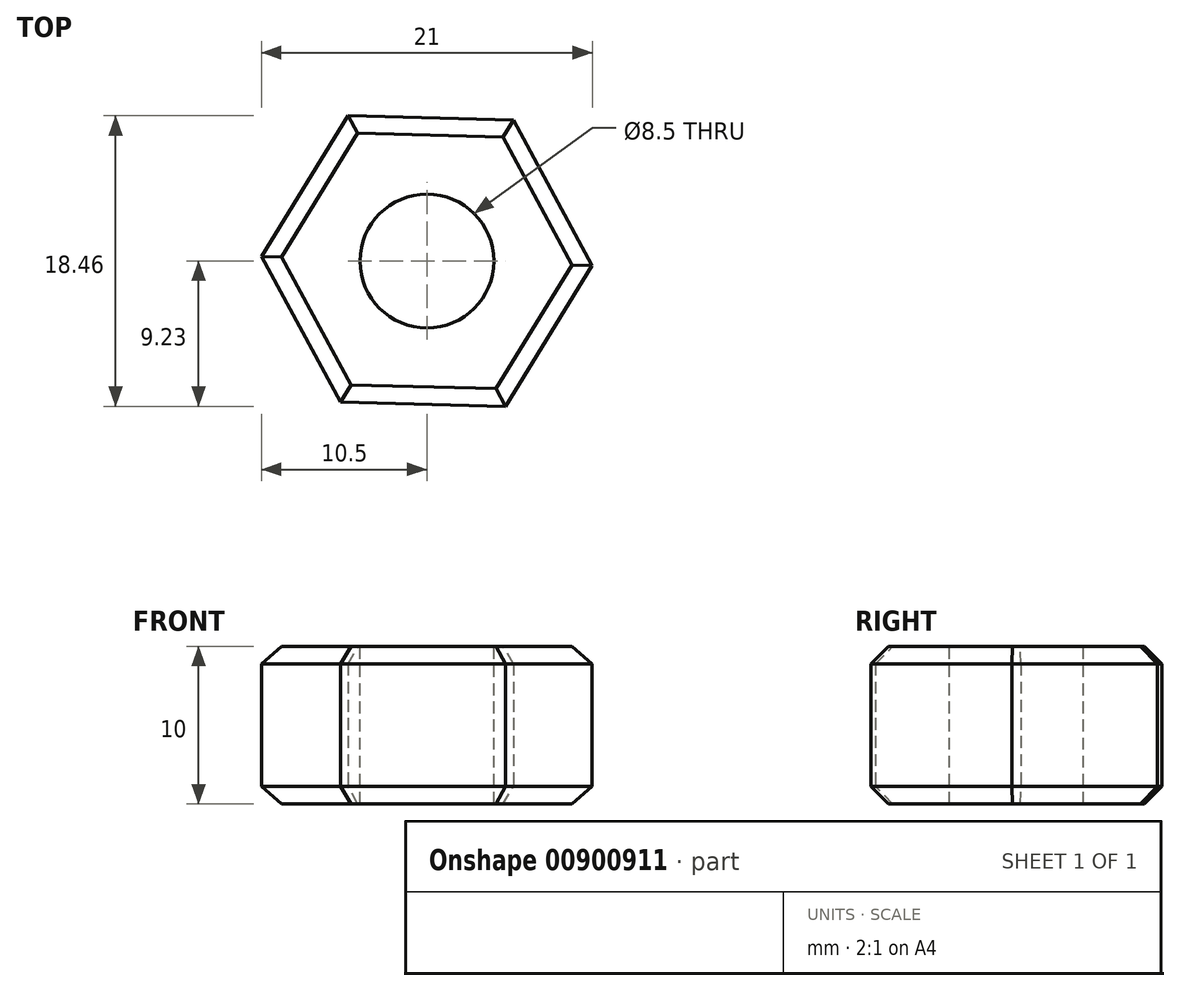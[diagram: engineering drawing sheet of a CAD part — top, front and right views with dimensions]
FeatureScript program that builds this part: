
annotation { "Feature Type Name" : "Feature", "Feature Type Description" : "" }
export const myFeature = defineFeature(function(context is Context, id is Id, definition is map)
    precondition{}
    {
        {
            var Q0;
            Q0=qCreatedBy(makeId("Top.planeOp"),FACE);
            var sketch = newSketch(context, id + "F0", { "sketchPlane" : qUnion([Q0])});
            skCircle(sketch, "E0.cCircle", {"center": v(0, 0) * mm, "radius": 10.5 * mm, "construction": true});
            skLineSegment(sketch, "E0.0", {"start": v(5.5, 8.95) * mm, "end": v(10.5, -0.28) * mm});
            skLineSegment(sketch, "E0.1", {"start": v(10.5, -0.28) * mm, "end": v(5, -9.23) * mm});
            skLineSegment(sketch, "E0.2", {"start": v(5, -9.23) * mm, "end": v(-5.5, -8.95) * mm});
            skLineSegment(sketch, "E0.3", {"start": v(-5.5, -8.95) * mm, "end": v(-10.5, 0.28) * mm});
            skLineSegment(sketch, "E0.4", {"start": v(-10.5, 0.28) * mm, "end": v(-5, 9.23) * mm});
            skLineSegment(sketch, "E0.5", {"start": v(-5, 9.23) * mm, "end": v(5.5, 8.95) * mm});
            skSolve(sketch);
        }
        {
            var Q0;
            Q0 = qSketchRegion(id + "F0", true);
            extrude(context, id + "F1", {"entities" : qUnion([Q0]), "depth" : 10 * mm, "offsetDistance" : 25 * mm});
        }
        {
            var Q0;
            Q0=makeQuery(id+"F1.opExtrude","CAP_FACE",FACE,{"disambiguationData":[OSD([sQuery(id+"F0.wireOp",EDGE,"E0.0"),sQuery(id+"F0.wireOp",EDGE,"E0.1"),sQuery(id+"F0.wireOp",EDGE,"E0.2"),sQuery(id+"F0.wireOp",EDGE,"E0.3"),sQuery(id+"F0.wireOp",EDGE,"E0.4"),sQuery(id+"F0.wireOp",EDGE,"E0.5")])],"isStart":false});
            var sketch = newSketch(context, id + "F2", { "sketchPlane" : qUnion([Q0])});
            skLineSegment(sketch, "E1", {"start": v(0, 0) * mm, "end": v(-5.5, -8.95) * mm, "construction": true});
            skSolve(sketch);
        }
        {
            var Q0;
            Q0=sQuery(id+"F2.wireOp",VERTEX,"E1.start");
            var Q1;
            Q1=makeQuery(id+"F1.opExtrude","SWEPT_BODY",BODY,{"disambiguationData":[OSD([sQuery(id+"F0.wireOp",EDGE,"E0.0"),sQuery(id+"F0.wireOp",EDGE,"E0.1"),sQuery(id+"F0.wireOp",EDGE,"E0.2"),sQuery(id+"F0.wireOp",EDGE,"E0.3"),sQuery(id+"F0.wireOp",EDGE,"E0.4"),sQuery(id+"F0.wireOp",EDGE,"E0.5")])]});
            hole(context, id + "F3", {"style" : HoleStyle.SIMPLE, "endStyle" : HoleEndStyle.THROUGH, "standardTappedOrClearance" : lookupTablePath({ "standard" : "ISO", "engagement" : "75%", "pitch" : "1.5 mm", "size" : "M10", "type" : "Tapped" }), "standardBlindInLast" : lookupTablePath({ "standard" : "ISO", "engagement" : "75%", "pitch" : "1.5 mm", "size" : "M10", "type" : "Tapped" }), "holeDiameter" : 8.5 * mm, "majorDiameter" : 10 * mm, "showTappedDepth" : true, "isTappedThrough" : true, "tappedDepth" : 12 * mm, "tapClearance" : 3, "locations" : qUnion([Q0]), "scope" : qUnion([Q1])});
        }
        {
            var Q0;
            Q0=makeQuery(id+"F1.opExtrude","CAP_EDGE",EDGE,{"disambiguationData":[OSD([sQuery(id+"F0.wireOp",EDGE,"E0.3")])],"isStart":false});
            var Q1;
            Q1=makeQuery(id+"F1.opExtrude","CAP_EDGE",EDGE,{"disambiguationData":[OSD([sQuery(id+"F0.wireOp",EDGE,"E0.4")])],"isStart":false});
            var Q2;
            Q2=makeQuery(id+"F1.opExtrude","CAP_EDGE",EDGE,{"disambiguationData":[OSD([sQuery(id+"F0.wireOp",EDGE,"E0.5")])],"isStart":false});
            var Q3;
            Q3=makeQuery(id+"F1.opExtrude","CAP_EDGE",EDGE,{"disambiguationData":[OSD([sQuery(id+"F0.wireOp",EDGE,"E0.0")])],"isStart":false});
            var Q4;
            Q4=makeQuery(id+"F1.opExtrude","CAP_EDGE",EDGE,{"disambiguationData":[OSD([sQuery(id+"F0.wireOp",EDGE,"E0.1")])],"isStart":false});
            var Q5;
            Q5=makeQuery(id+"F1.opExtrude","CAP_EDGE",EDGE,{"disambiguationData":[OSD([sQuery(id+"F0.wireOp",EDGE,"E0.2")])],"isStart":false});
            var Q6;
            Q6=makeQuery(id+"F1.opExtrude","CAP_EDGE",EDGE,{"disambiguationData":[OSD([sQuery(id+"F0.wireOp",EDGE,"E0.2")])],"isStart":true});
            var Q7;
            Q7=makeQuery(id+"F1.opExtrude","CAP_EDGE",EDGE,{"disambiguationData":[OSD([sQuery(id+"F0.wireOp",EDGE,"E0.1")])],"isStart":true});
            var Q8;
            Q8=makeQuery(id+"F1.opExtrude","CAP_EDGE",EDGE,{"disambiguationData":[OSD([sQuery(id+"F0.wireOp",EDGE,"E0.0")])],"isStart":true});
            var Q9;
            Q9=makeQuery(id+"F1.opExtrude","CAP_EDGE",EDGE,{"disambiguationData":[OSD([sQuery(id+"F0.wireOp",EDGE,"E0.5")])],"isStart":true});
            var Q10;
            Q10=makeQuery(id+"F1.opExtrude","CAP_EDGE",EDGE,{"disambiguationData":[OSD([sQuery(id+"F0.wireOp",EDGE,"E0.4")])],"isStart":true});
            var Q11;
            Q11=makeQuery(id+"F1.opExtrude","CAP_EDGE",EDGE,{"disambiguationData":[OSD([sQuery(id+"F0.wireOp",EDGE,"E0.3")])],"isStart":true});
            chamfer(context, id + "F4", {"entities" : qUnion([Q0, Q1, Q2, Q3, Q4, Q5, Q6, Q7, Q8, Q9, Q10, Q11]), "width" : 1.1 * mm, "tangentPropagation" : true});
        }
    });
